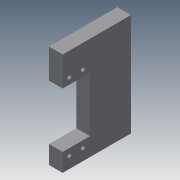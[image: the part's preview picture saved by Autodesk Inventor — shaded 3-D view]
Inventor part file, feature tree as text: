
AUTODESK INVENTOR PART (.ipt)
format: ipt  version: 2013 (Build 170138000, 138)  size: 429,056 bytes
history: native  units: mm
features: extrude x33, sketch x33, fillet x1
ambient origin geometry x8: Origin, YZ Plane, XZ Plane, XY Plane, X Axis, Y Axis, Z Axis, Center Point
bodies: Solid1 (feature_tree)
feature tree (67):
  extrude  "Extrusion1"  Depth=6.0mm
  extrude  "Extrusion2"  Depth=24.3mm
  extrude  "Extrusion3"  Depth=24.3mm
  extrude  "Extrusion4"  Depth=10.0mm
  sketch  "Sketch5"  dims[d9=60.0mm d10=60.0mm]
  extrude  "Extrusion5"  Depth=60.0mm
  extrude  "Extrusion6"  Depth=15.0mm
  extrude  "Extrusion7"  Depth=15.0mm
  extrude  "Extrusion8"  Depth=3.0mm
  extrude  "Extrusion9"  Depth=3.0mm
  extrude  "Extrusion10"  Depth=71.2mm
  extrude  "Extrusion11"  Depth=55.0mm
  extrude  "Extrusion12"  Depth=10.0mm
  extrude  "Extrusion13"  Depth=5.0mm TaperAngle=0.0deg
  extrude  "Extrusion15"  Depth=4.0mm
  extrude  "Extrusion16"  Depth=48.0mm TaperAngle=0.0deg
  extrude  "Extrusion17"  Depth=34.25mm
  extrude  "Extrusion22"  Depth=40.2mm
  sketch  "Sketch24"  dims[d55=49.7mm d56=40.2mm]
  sketch  "Sketch25"  dims[d60=3.0mm d61=3.0mm]
  extrude  "Extrusion23"  Depth=3.0mm
  extrude  "Extrusion24"  Depth=3.0mm
  sketch  "Sketch29"  dims[d64=10.0mm d65=0.0mm d66=3.0mm d67=0.0mm]
  extrude  "Extrusion28"  Depth=3.0mm TaperAngle=0.0deg
  extrude  "Extrusion29"  Depth=4.0mm
  extrude  "Extrusion30"  Depth=8.0mm
  extrude  "Extrusion31"  Depth=15.0mm
  extrude  "Extrusion32"  Depth=6.0mm TaperAngle=0.0deg
  extrude  "Extrusion33"  Depth=14.3mm
  extrude  "Extrusion34"  Depth=48.6mm
  extrude  "Extrusion35"  Depth=35.0mm
  fillet  "Fillet9"  Radius=14.3mm
  extrude  "Extrusion36"  Depth=24.0mm TaperAngle=0.0deg
  extrude  "Extrusion37"  Depth=4.589mm
  sketch  "Sketch41"  dims[d102=4.589mm d103=10.0mm d104=0.0mm]
  extrude  "Extrusion38"  Depth=19.125mm
  extrude  "Extrusion39"  Depth=10.0mm TaperAngle=0.0deg
  extrude  "Extrusion40"  Depth=10.0mm TaperAngle=0.0deg
  extrude  "Extrusion41"  Depth=2.0mm TaperAngle=0.0deg
  sketch  "Sketch1"  dims[d0=120.0mm d1=6.0mm]
  sketch  "Sketch2"  dims[d2=10.0mm d3=0.0mm d4=24.3mm]
  sketch  "Sketch3"  dims[d5=5.0mm d6=24.3mm]
  sketch  "Sketch4"  dims[d7=5.0mm d8=10.0mm]
  sketch  "Sketch6"  dims[d11=15.0mm d12=15.0mm]
  sketch  "Sketch7"  dims[d13=15.0mm d14=15.0mm]
  sketch  "Sketch8"  dims[d15=3.0mm d16=3.0mm]
  sketch  "Sketch9"  dims[d17=3.0mm d18=3.0mm]
  sketch  "Sketch10"  dims[d19=10.0mm d20=0.0mm d31=71.2mm]
  sketch  "Sketch11"  dims[d32=34.25mm d33=55.0mm]
  sketch  "Sketch12"  dims[d34=10.0mm d35=0.0mm d36=10.0mm]
  sketch  "Sketch14"  dims[d37=43.0mm d38=0.0mm d41=5.0mm d42=0.0mm]
  sketch  "Sketch16"  dims[d45=4.0mm d46=4.0mm]
  sketch  "Sketch18"  dims[d47=10.0mm d48=0.0mm d49=48.0mm d50=0.0mm]
  sketch  "Sketch23"  dims[d51=35.0mm d54=34.25mm]
  sketch  "Sketch26"  dims[d62=3.0mm d63=3.0mm]
  sketch  "Sketch31"  dims[d70=14.209mm d71=4.0mm]
  sketch  "Sketch32"  dims[d72=10.0mm d73=0.0mm d74=8.0mm]
  sketch  "Sketch33"  dims[d75=10.0mm d76=0.0mm d78=15.0mm]
  sketch  "Sketch34"  dims[d79=10.0mm d80=6.0mm d81=0.0mm]
  sketch  "Sketch35"  dims[d82=14.3mm d83=14.3mm]
  sketch  "Sketch36"  dims[d84=6.0mm d85=0.0mm d90=48.6mm]
  sketch  "Sketch37"  dims[d91=14.3mm d92=35.0mm d93=14.3mm]
  sketch  "Sketch38"  dims[d94=35.0mm d95=24.0mm d96=0.0mm]
  sketch  "Sketch39"  dims[d97=19.125mm d98=4.589mm]
  sketch  "Sketch40"  dims[d99=10.0mm d100=0.0mm d101=19.125mm]
  sketch  "Sketch42"  dims[d123=15.0mm d124=10.0mm d125=0.0mm]
  sketch  "Sketch43"  dims[d126=35.0mm d129=2.0mm d130=0.0mm d131=10.0mm d132=2.0mm d133=0.0mm d144=7.5mm d145=10.0mm d146=0.0mm d147=3.0mm d148=6.0mm d149=2.0mm d150=10.0mm d151=0.0mm d152=24.0mm d153=0.0mm d154=24.0mm d155=0.0mm d156=6.0mm d157=0.0mm d158=15.0mm d159=24.0mm d160=6.0mm d161=0.0mm d162=16.0mm d163=20.0mm d164=6.0mm d165=0.0mm d166=17.0mm d167=6.0mm d168=0.0mm d169=2.0mm d170=2.0mm d171=0.0mm d172=10.0mm d173=0.0mm d174=10.0mm d175=0.0mm d176=10.0mm d177=0.0mm d178=37.5mm d179=75.0mm d180=10.0mm d181=0.0mm d182=5.0mm d183=0.0mm]
